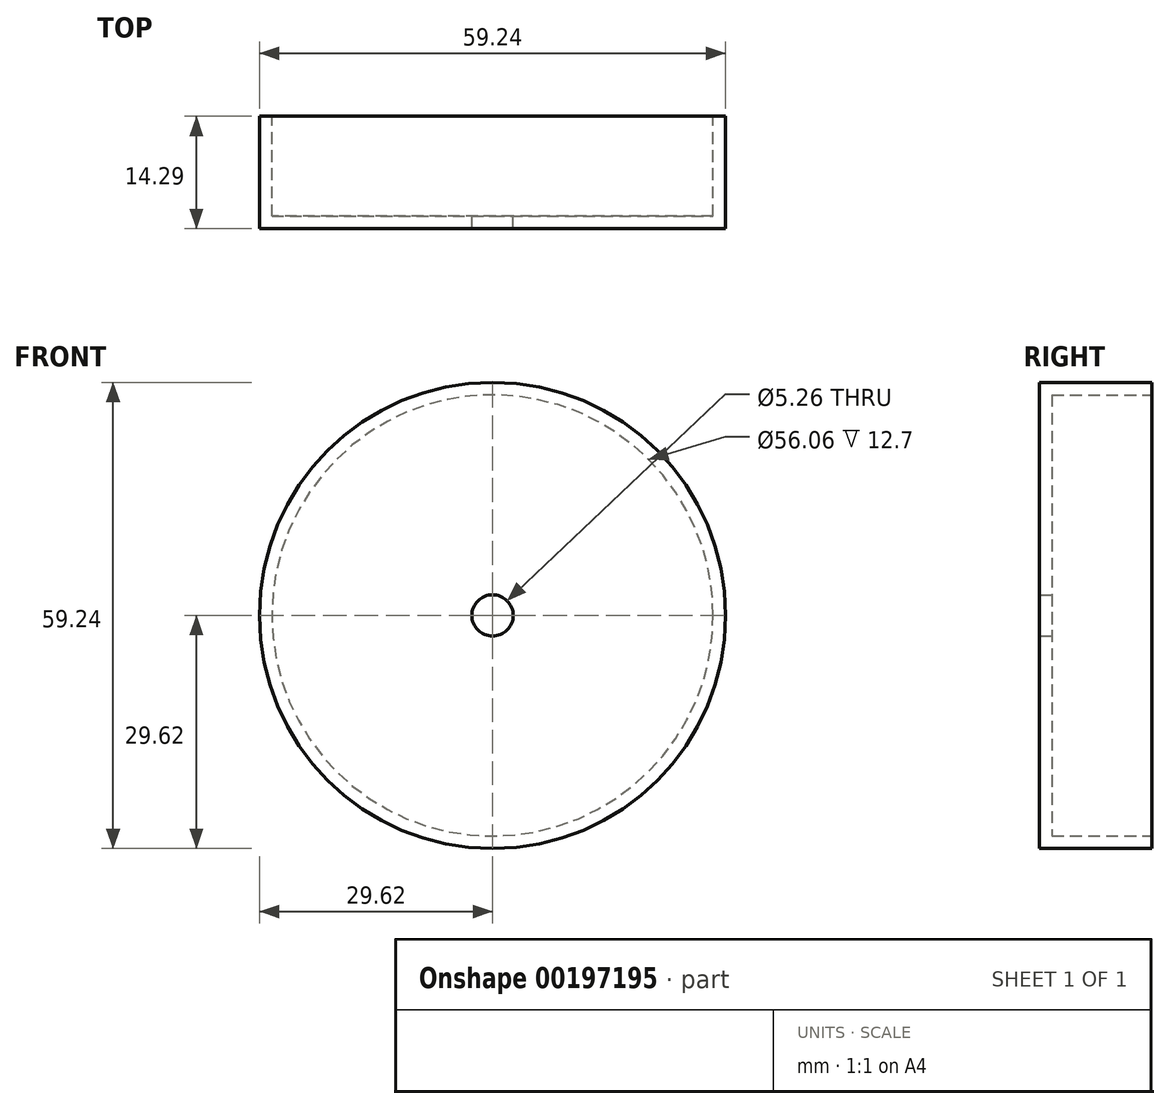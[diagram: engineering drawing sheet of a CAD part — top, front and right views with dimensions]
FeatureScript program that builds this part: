
annotation { "Feature Type Name" : "Feature", "Feature Type Description" : "" }
export const myFeature = defineFeature(function(context is Context, id is Id, definition is map)
    precondition{}
    {
        {
            var Q0;
            Q0=qCreatedBy(makeId("Top.planeOp"),FACE);
            var sketch = newSketch(context, id + "F0", { "sketchPlane" : qUnion([Q0])});
            skLineSegment(sketch, "E0", {"start": v(2.63, 0) * mm, "end": v(2.63, 1.59) * mm});
            skLineSegment(sketch, "E1", {"start": v(2.63, 1.59) * mm, "end": v(28.03, 1.59) * mm});
            skLineSegment(sketch, "E2", {"start": v(28.03, 1.59) * mm, "end": v(28.03, 14.29) * mm});
            skLineSegment(sketch, "E3", {"start": v(28.03, 14.29) * mm, "end": v(29.62, 14.29) * mm});
            skLineSegment(sketch, "E4", {"start": v(29.62, 14.29) * mm, "end": v(29.62, 0) * mm});
            skLineSegment(sketch, "E5", {"start": v(0, 28.36) * mm, "end": v(0, 0) * mm});
            skLineSegment(sketch, "E6", {"start": v(0, 0) * mm, "end": v(37.08, 0) * mm});
            skSolve(sketch);
        }
        {
            var Q0;
            Q0 = qSketchRegion(id + "F0", true);
            var Q1;
            Q1=sQuery(id+"F0.wireOp",EDGE,"E5");
            revolve(context, id + "F1", {"entities" : qUnion([Q0]), "axis" : qUnion([Q1]), "revolveType" : RevolveType.FULL});
        }
    });
